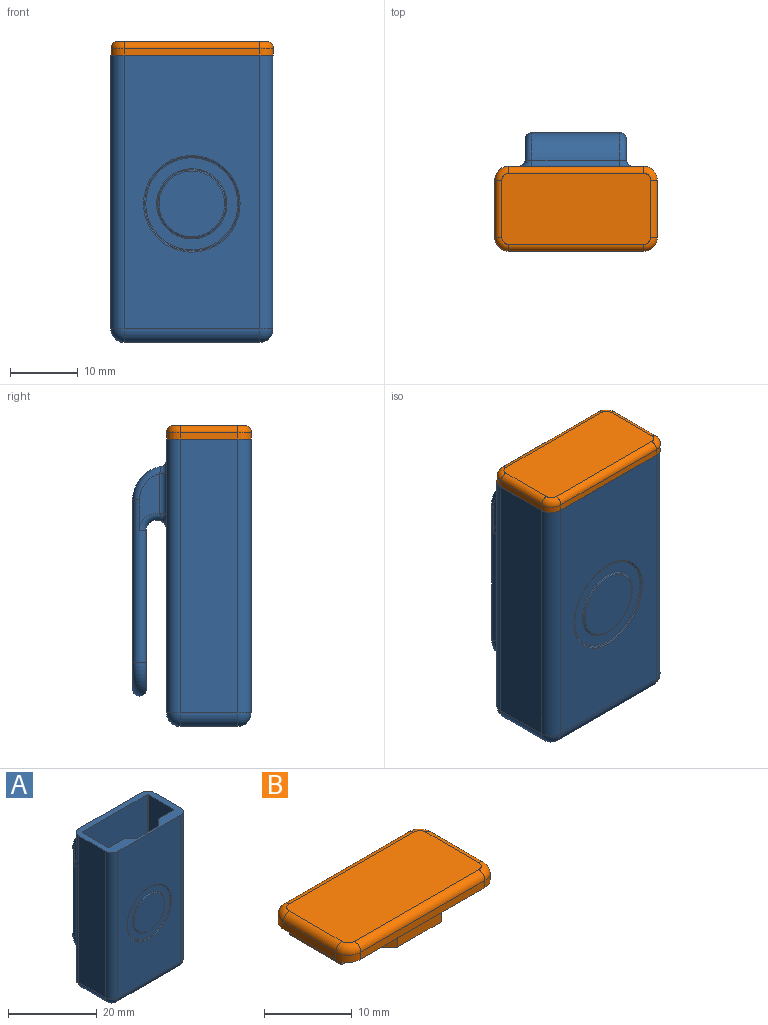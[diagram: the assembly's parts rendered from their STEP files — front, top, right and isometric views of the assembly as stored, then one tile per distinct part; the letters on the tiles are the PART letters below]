
ASSEMBLY  parts=2 mates=1
PART A: 79 faces, bbox 24.1x18x42.6 mm
  f0: plane 28x13mm, normal (0,1,0), area 240.6mm2, adj f53,f54,f55,f56,f57,f60,f61,f62
  f1: plane 23.5x13mm, normal (0,-1,0), area 182.1mm2, adj f53,f54,f55,f56,f58,f60,f61,f62
  f2: plane 40.8x20.6mm, normal (0,1,0), area 358.1mm2, adj f3,f13,f15,f16,f19,f39,f40,f41
  f3: plane 24x12.5mm, normal (0,0,1), area 100.1mm2, adj f2,f4,f5,f6,f7,f9,f10,f11
  f4: plane 40.5x8.5mm, normal (1,0,0), area 344.3mm2, adj f3,f27,f30,f34
  f5: plane 40.5x20mm, normal (0,1,0), area 637.5mm2, adj f3,f27,f28,f31,f58,f72,f73,f74
  f6: plane 40.5x8.5mm, normal (-1,0,0), area 344.3mm2, adj f3,f28,f29,f35
  f7: plane 40.5x20mm, normal (0,-1,0), area 649.6mm2, adj f3,f29,f30,f38,f50
  f8: plane 20x8.5mm, normal (0,0,-1), area 170mm2, adj f31,f34,f35,f38
  f9: plane 40.8x8.1mm, normal (-1,0,0), area 330.5mm2, adj f3,f16,f18,f22
  f10: plane 40.8x20.6mm, normal (0,-1,0), area 840.5mm2, adj f3,f17,f18,f26
  f11: plane 40.8x8.1mm, normal (1,0,0), area 330.5mm2, adj f3,f15,f17,f23
  f12: plane 20.6x8.1mm, normal (0,0,1), area 166.9mm2, adj f19,f22,f23,f26
  f13: plane 11x2mm, normal (0,0,1), area 18mm2, adj f2,f14,f40,f42
  f14: plane 37.53x14mm, normal (0,1,0), area 322.9mm2, adj f3,f13,f39,f40,f41,f42,f43,f44
  f15: cylinder r=0.2mm len=40.8mm, axis (0,0,-1), area 12.8mm2, adj f2,f3,f11,f21
  f16: cylinder r=0.2mm len=40.8mm, axis (0,0,1), area 12.8mm2, adj f2,f3,f9,f20
  f17: cylinder r=0.2mm len=40.8mm, axis (0,0,1), area 12.8mm2, adj f3,f10,f11,f25
  f18: cylinder r=0.2mm len=40.8mm, axis (0,0,-1), area 12.8mm2, adj f3,f9,f10,f24
  f19: cylinder r=0.2mm len=20.6mm, axis (-1,0,0), area 6.5mm2, adj f2,f12,f20,f21
  f20: sphere r=0.2mm, area 0.1mm2, adj f16,f19,f22
  f21: sphere r=0.2mm, area 0.1mm2, adj f15,f19,f23
  f22: cylinder r=0.2mm len=8.1mm, axis (0,-1,0), area 2.5mm2, adj f9,f12,f20,f24
  f23: cylinder r=0.2mm len=8.1mm, axis (0,1,0), area 2.5mm2, adj f11,f12,f21,f25
  f24: sphere r=0.2mm, area 0.1mm2, adj f18,f22,f26
  f25: sphere r=0.2mm, area 0.1mm2, adj f17,f23,f26
  f26: cylinder r=0.2mm len=20.6mm, axis (1,0,0), area 6.5mm2, adj f10,f12,f24,f25
  f27: cylinder r=2mm len=40.5mm, axis (0,0,1), area 127.2mm2, adj f3,f4,f5,f32
  f28: cylinder r=2mm len=40.5mm, axis (0,0,-1), area 127.2mm2, adj f3,f5,f6,f33
  f29: cylinder r=2mm len=40.5mm, axis (0,0,1), area 127.2mm2, adj f3,f6,f7,f37
  f30: cylinder r=2mm len=40.5mm, axis (0,0,-1), area 127.2mm2, adj f3,f4,f7,f36
  f31: cylinder r=2mm len=20mm, axis (-1,0,0), area 62.8mm2, adj f5,f8,f32,f33
  f32: sphere r=2mm, area 6.3mm2, adj f27,f31,f34
  f33: sphere r=2mm, area 6.3mm2, adj f28,f31,f35
  f34: cylinder r=2mm len=8.5mm, axis (0,1,0), area 26.7mm2, adj f4,f8,f32,f36
  f35: cylinder r=2mm len=8.5mm, axis (0,-1,0), area 26.7mm2, adj f6,f8,f33,f37
  f36: sphere r=2mm, area 6.3mm2, adj f30,f34,f38
  f37: sphere r=2mm, area 6.3mm2, adj f29,f35,f38
  f38: cylinder r=2mm len=20mm, axis (1,0,0), area 62.8mm2, adj f7,f8,f36,f37
  f39: plane 16.04x2.11mm, normal (-0.71,0.71,0), area 43.5mm2, adj f2,f3,f14,f41
  f40: plane 9.57x2.11mm, normal (-0.71,0.71,0), area 25.2mm2, adj f2,f13,f14,f41
  f41: cone r=7mm half-angle=45deg, axis (0,1,0), area 44.2mm2, adj f2,f14,f39,f40
  f42: plane 9.57x2.11mm, normal (0.71,0.71,0), area 25.2mm2, adj f2,f13,f14,f44
  f43: plane 16.04x2.11mm, normal (0.71,0.71,0), area 43.5mm2, adj f2,f3,f14,f44
  f44: cone r=7mm half-angle=45deg, axis (0,1,0), area 44.2mm2, adj f2,f14,f42,f43
  f45: plane 13.6x13.6mm, normal (0,-1,0), area 60.3mm2, adj f47,f48
  f46: plane 9.71x9.71mm, normal (0,-1,0), area 74mm2, adj f49
  f47: torus R=5.2mm, axis (0,-1,0), area 6.7mm2, adj f45,f49
  f48: torus R=6.8mm, axis (0,-1,0), area 9.1mm2, adj f45,f50
  f49: torus R=4.85mm, axis (0,1,0), area 6.5mm2, adj f46,f47
  f50: torus R=7.15mm, axis (0,-1,0), area 9.3mm2, adj f7,f48
  f51: plane 8.37x3mm, normal (1,0,0), area 16mm2, adj f64,f65,f71,f77
  f52: plane 8.37x3mm, normal (-1,0,0), area 16mm2, adj f59,f60,f70,f73
  f53: plane 16x2mm, normal (-1,0,0), area 32mm2, adj f0,f1,f66,f68
  f54: plane 2x2mm, normal (0,0,1), area 4mm2, adj f0,f1,f66,f67
  f55: plane 16x2mm, normal (1,0,0), area 32mm2, adj f0,f1,f67,f69
  f56: plane 2x2mm, normal (0,0,-1), area 4mm2, adj f0,f1,f68,f69
  f57: cylinder r=5mm len=13mm, axis (-1,0,0), area 91.2mm2, adj f0,f59,f65,f75
  f58: cylinder r=1.5mm len=13mm, axis (1,0,0), area 61.3mm2, adj f1,f5,f70,f71
  f59: torus R=4mm, axis (1,0,0), area 10mm2, adj f52,f57,f60,f74
  f60: cylinder r=1mm len=24mm, axis (0,0,1), area 68.3mm2, adj f0,f1,f52,f59,f61,f70
  f61: torus R=4mm, axis (0,-1,0), area 22.9mm2, adj f0,f1,f60,f62
  f62: cylinder r=1mm len=5mm, axis (1,0,0), area 15.7mm2, adj f0,f1,f61,f63
  f63: torus R=4mm, axis (0,-1,0), area 22.9mm2, adj f0,f1,f62,f64
  f64: cylinder r=1mm len=24mm, axis (0,0,-1), area 68.3mm2, adj f0,f1,f51,f63,f65,f71
  f65: torus R=4mm, axis (1,0,0), area 10mm2, adj f51,f57,f64,f76
  f66: cylinder r=2mm len=2mm, axis (0,1,0), area 6.3mm2, adj f0,f1,f53,f54
  f67: cylinder r=2mm len=2mm, axis (0,-1,0), area 6.3mm2, adj f0,f1,f54,f55
  f68: cylinder r=2mm len=2mm, axis (0,-1,0), area 6.3mm2, adj f0,f1,f53,f56
  f69: cylinder r=2mm len=2mm, axis (0,1,0), area 6.3mm2, adj f0,f1,f55,f56
  f70: torus R=2.5mm, axis (1,0,0), area 6.2mm2, adj f52,f58,f60,f72
  f71: torus R=2.5mm, axis (1,0,0), area 6.2mm2, adj f51,f58,f64,f78
  f72: bspline ~2.87x2mm, area 2.8mm2, adj f5,f70,f73
  f73: cylinder r=1mm len=5.92mm, axis (0,0,1), area 9.3mm2, adj f5,f52,f72,f74
  f74: bspline ~2.53x2.44mm, area 3.2mm2, adj f5,f59,f73,f75
  f75: cylinder r=1mm len=13mm, axis (-1,0,0), area 18.2mm2, adj f5,f57,f74,f76
  f76: bspline ~2.53x2.44mm, area 3.2mm2, adj f5,f65,f75,f77
  f77: cylinder r=1mm len=5.92mm, axis (0,0,-1), area 9.3mm2, adj f5,f51,f76,f78
  f78: bspline ~2.87x2mm, area 2.8mm2, adj f5,f71,f77
PART B: 36 faces, bbox 24.3x12.8x3.8 mm
  f0: plane 24x12.5mm, normal (0,0,-1), area 100.1mm2, adj f1,f2,f3,f4,f6,f7,f8,f9
  f1: plane 20x1mm, normal (0,1,0), area 20mm2, adj f0,f6,f9,f28
  f2: plane 8.5x1mm, normal (-1,0,0), area 8.5mm2, adj f0,f6,f7,f31
  f3: plane 20x1mm, normal (0,-1,0), area 20mm2, adj f0,f7,f8,f35
  f4: plane 8.5x1mm, normal (1,0,0), area 8.5mm2, adj f0,f8,f9,f32
  f5: plane 22x10.5mm, normal (0,0,1), area 230.1mm2, adj f28,f29,f30,f31,f32,f33,f34,f35
  f6: cylinder r=2mm len=2mm, axis (0,0,1), area 3.1mm2, adj f0,f1,f2,f29
  f7: cylinder r=2mm len=2mm, axis (0,0,-1), area 3.1mm2, adj f0,f2,f3,f33
  f8: cylinder r=2mm len=2mm, axis (0,0,1), area 3.1mm2, adj f0,f3,f4,f34
  f9: cylinder r=2mm len=2mm, axis (0,0,-1), area 3.1mm2, adj f0,f1,f4,f30
  f10: plane 5x1.8mm, normal (0,-1,0), area 9mm2, adj f0,f11,f17,f18
  f11: plane 2x2mm, normal (0.71,-0.71,0), area 5.1mm2, adj f0,f10,f12,f18
  f12: plane 7x1.8mm, normal (0,-1,0), area 12.6mm2, adj f0,f11,f13,f18
  f13: plane 2x2mm, normal (-0.71,-0.71,0), area 5.1mm2, adj f0,f12,f14,f18
  f14: plane 5x1.8mm, normal (0,-1,0), area 9mm2, adj f0,f13,f15,f18
  f15: plane 8.5x1.8mm, normal (-1,0,0), area 15.3mm2, adj f0,f14,f16,f18
  f16: plane 21x1.8mm, normal (0,1,0), area 37.8mm2, adj f0,f15,f17,f18
  f17: plane 8.5x1.8mm, normal (1,0,0), area 15.3mm2, adj f0,f10,f16,f18
  f18: plane 21x10.5mm, normal (0,0,-1), area 29.3mm2, adj f10,f11,f12,f13,f14,f15,f16,f17
  f19: plane 4.71x2mm, normal (0,1,0), area 9.4mm2, adj f18,f20,f26,f27
  f20: plane 2x2mm, normal (-0.71,0.71,0), area 5.7mm2, adj f18,f19,f21,f27
  f21: plane 6.59x2mm, normal (0,1,0), area 13.2mm2, adj f18,f20,f22,f27
  f22: plane 2x2mm, normal (0.71,0.71,0), area 5.7mm2, adj f18,f21,f23,f27
  f23: plane 4.71x2mm, normal (0,1,0), area 9.4mm2, adj f18,f22,f24,f27
  f24: plane 7.5x2mm, normal (1,0,0), area 15mm2, adj f18,f23,f25,f27
  f25: plane 20x2mm, normal (0,-1,0), area 40mm2, adj f18,f24,f26,f27
  f26: plane 7.5x2mm, normal (-1,0,0), area 15mm2, adj f18,f19,f25,f27
  f27: plane 20x9.5mm, normal (0,0,-1), area 167.2mm2, adj f19,f20,f21,f22,f23,f24,f25,f26
  f28: cylinder r=1mm len=20mm, axis (1,0,0), area 31.4mm2, adj f1,f5,f29,f30
  f29: torus R=1mm, axis (0,0,1), area 4mm2, adj f5,f6,f28,f31
  f30: torus R=1mm, axis (0,0,1), area 4mm2, adj f5,f9,f28,f32
  f31: cylinder r=1mm len=8.5mm, axis (0,1,0), area 13.4mm2, adj f2,f5,f29,f33
  f32: cylinder r=1mm len=8.5mm, axis (0,-1,0), area 13.4mm2, adj f4,f5,f30,f34
  f33: torus R=1mm, axis (0,0,1), area 4mm2, adj f5,f7,f31,f35
  f34: torus R=1mm, axis (0,0,1), area 4mm2, adj f5,f8,f32,f35
  f35: cylinder r=1mm len=20mm, axis (-1,0,0), area 31.4mm2, adj f3,f5,f33,f34
PLACE A t=(0,0,1.01)mm
PLACE B t=(0.06,-0.53,42.01)mm
MATE planar B.f0 <-> A.f3  axis (0,0,-1) through (0.06,-0.68,42.01)mm
